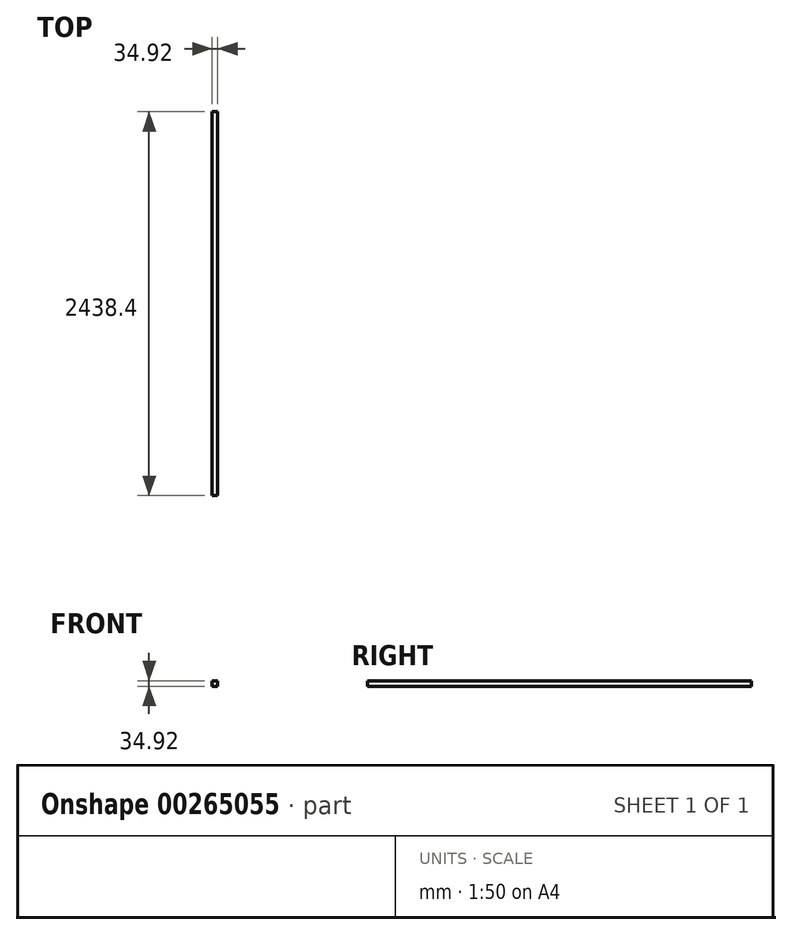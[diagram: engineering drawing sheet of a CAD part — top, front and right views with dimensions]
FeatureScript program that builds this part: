
annotation { "Feature Type Name" : "Feature", "Feature Type Description" : "" }
export const myFeature = defineFeature(function(context is Context, id is Id, definition is map)
    precondition{}
    {
        {
            var Q0;
            Q0=qCreatedBy(makeId("Front.planeOp"),FACE);
            var sketch = newSketch(context, id + "F0", { "sketchPlane" : qUnion([Q0])});
            skLineSegment(sketch, "E0.bottom", {"start": v(17.46, 17.46) * mm, "end": v(-17.46, 17.46) * mm});
            skLineSegment(sketch, "E0.top", {"start": v(17.46, -17.46) * mm, "end": v(-17.46, -17.46) * mm});
            skLineSegment(sketch, "E0.left", {"start": v(17.46, 17.46) * mm, "end": v(17.46, -17.46) * mm});
            skLineSegment(sketch, "E0.right", {"start": v(-17.46, 17.46) * mm, "end": v(-17.46, -17.46) * mm});
            skPoint(sketch, "E0.middle", {"position": v(0, 0) * mm});
            skSolve(sketch);
        }
        {
            var Q0;
            Q0 = qSketchRegion(id + "F0", true);
            extrude(context, id + "F1", {"entities" : qUnion([Q0]), "depth" : 2438.4 * mm});
        }
    });
